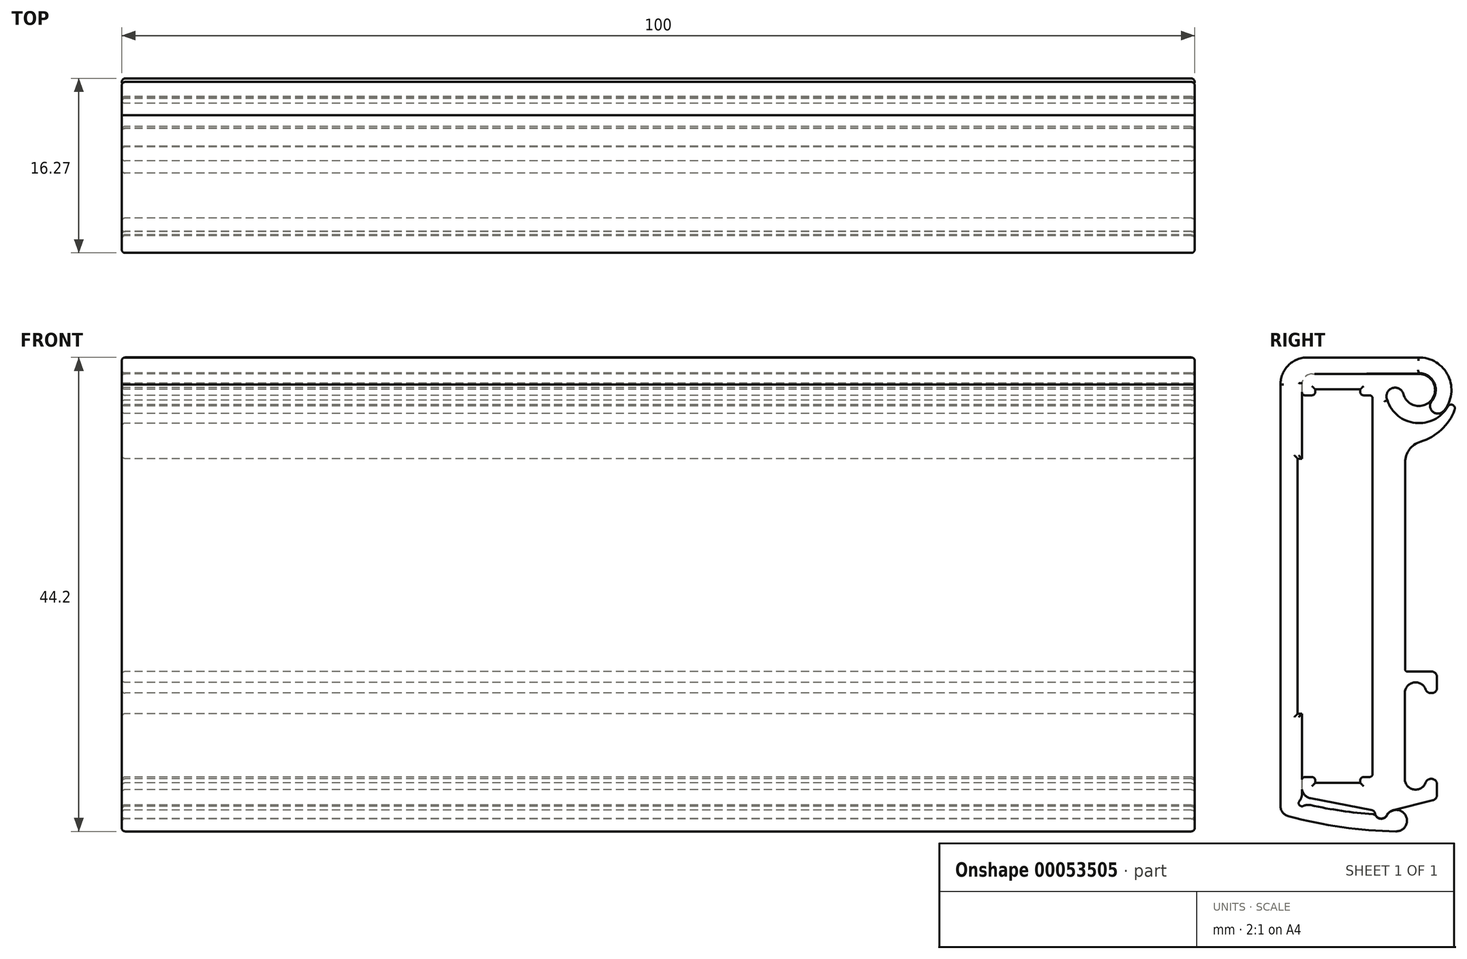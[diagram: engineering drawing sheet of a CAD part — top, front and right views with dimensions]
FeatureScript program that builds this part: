
annotation { "Feature Type Name" : "Feature", "Feature Type Description" : "" }
export const myFeature = defineFeature(function(context is Context, id is Id, definition is map)
    precondition{}
    {
        {
            var Q0;
            Q0=qCreatedBy(makeId("Right.planeOp"),FACE);
            var sketch = newSketch(context, id + "F0", { "sketchPlane" : qUnion([Q0])});
            skLineSegment(sketch, "E0.bottom", {"start": v(-0.5, 35) * mm, "end": v(-6, 35) * mm});
            skLineSegment(sketch, "E0.top", {"start": v(-0.5, 0) * mm, "end": v(-6, 0) * mm});
            skLineSegment(sketch, "E0.left", {"start": v(0, 34.5) * mm, "end": v(0, 0.5) * mm});
            skLineSegment(sketch, "E0.right", {"start": v(-6.5, 34.5) * mm, "end": v(-6.5, 0.5) * mm});
            skPoint(sketch, "E1.visualSharp", {"position": v(0, 35) * mm});
            skArc(sketch, "E1.filletArc", {"start": v(0, 34.5) * mm, "mid": v(-0.15, 34.85) * mm, "end": v(-0.5, 35) * mm});
            skPoint(sketch, "E2.visualSharp", {"position": v(-6.5, 35) * mm});
            skArc(sketch, "E2.filletArc", {"start": v(-6, 35) * mm, "mid": v(-6.35, 34.85) * mm, "end": v(-6.5, 34.5) * mm});
            skPoint(sketch, "E3.visualSharp", {"position": v(-6.5, 0) * mm});
            skArc(sketch, "E3.filletArc", {"start": v(-6.5, 0.5) * mm, "mid": v(-6.35, 0.15) * mm, "end": v(-6, 0) * mm});
            skPoint(sketch, "E4.visualSharp", {"position": v(0, 0) * mm});
            skArc(sketch, "E4.filletArc", {"start": v(-0.5, 0) * mm, "mid": v(-0.15, 0.15) * mm, "end": v(0, 0.5) * mm});
            skLineSegment(sketch, "E5", {"start": v(-6.5, 17.5) * mm, "end": v(0, 17.5) * mm, "construction": true});
            skLineSegment(sketch, "E6.rect.bottom", {"start": v(-3.25, 35.5) * mm, "end": v(-3.25, 35.5) * mm});
            skLineSegment(sketch, "E6.rect.top", {"start": v(-2.25, 34.5) * mm, "end": v(-4.25, 34.5) * mm, "construction": true});
            skLineSegment(sketch, "E6.rect.left", {"start": v(-2.25, 34.5) * mm, "end": v(-2.25, 34.5) * mm});
            skLineSegment(sketch, "E6.rect.right", {"start": v(-4.25, 34.5) * mm, "end": v(-4.25, 34.5) * mm});
            skPoint(sketch, "E6.rect.middle", {"position": v(-3.25, 35) * mm});
            skPoint(sketch, "E7.visualSharp", {"position": v(-4.25, 35.5) * mm});
            skArc(sketch, "E7.filletArc", {"start": v(-3.25, 35.5) * mm, "mid": v(-3.96, 35.2) * mm, "end": v(-4.25, 34.5) * mm, "construction": true});
            skPoint(sketch, "E8.visualSharp", {"position": v(-2.25, 35.5) * mm});
            skArc(sketch, "E8.filletArc", {"start": v(-2.25, 34.5) * mm, "mid": v(-2.54, 35.2) * mm, "end": v(-3.25, 35.5) * mm, "construction": true});
            skPoint(sketch, "E9.MirrorP", {"position": v(-3.25, 0) * mm});
            skPoint(sketch, "E10.MirrorP", {"position": v(-2.25, -0.5) * mm});
            skArc(sketch, "E11.MirrorCS", {"start": v(-2.25, 0.5) * mm, "mid": v(-2.54, -0.2) * mm, "end": v(-3.25, -0.5) * mm, "construction": true});
            skPoint(sketch, "E12.MirrorP", {"position": v(-4.25, -0.5) * mm});
            skLineSegment(sketch, "E13.MirrorCS", {"start": v(-3.25, -0.5) * mm, "end": v(-3.25, -0.5) * mm});
            skArc(sketch, "E14.MirrorCS", {"start": v(-3.25, -0.5) * mm, "mid": v(-3.96, -0.2) * mm, "end": v(-4.25, 0.5) * mm, "construction": true});
            skLineSegment(sketch, "E15.MirrorCS", {"start": v(-4.25, 0.5) * mm, "end": v(-4.25, 0.5) * mm});
            skLineSegment(sketch, "E16.MirrorCS", {"start": v(-2.25, 0.5) * mm, "end": v(-4.25, 0.5) * mm, "construction": true});
            skLineSegment(sketch, "E17.MirrorCS", {"start": v(-2.25, 0.5) * mm, "end": v(-2.25, 0.5) * mm});
            skLineSegment(sketch, "E18.rect.bottom", {"start": v(-6, 29.4) * mm, "end": v(-6.5, 29.4) * mm});
            skLineSegment(sketch, "E18.rect.top", {"start": v(-6, 5.6) * mm, "end": v(-6.5, 5.6) * mm});
            skLineSegment(sketch, "E18.rect.left", {"start": v(-6, 29.4) * mm, "end": v(-6, 5.6) * mm, "construction": true});
            skPoint(sketch, "E18.rect.middle", {"position": v(-6.5, 17.5) * mm});
            skPoint(sketch, "E18.rect.right.end.orphan", {"position": v(-7, 5.6) * mm});
            skPoint(sketch, "E18.rect.right.start.orphan", {"position": v(-7, 29.4) * mm});
            skSolve(sketch);
        }
        {
            var Q0;
            Q0=qCreatedBy(makeId("Right.planeOp"),FACE);
            var sketch = newSketch(context, id + "F1", { "sketchPlane" : qUnion([Q0])});
            skLineSegment(sketch, "E19", {"start": v(-6.3, 35.3) * mm, "end": v(-5.65, 35.3) * mm});
            skLineSegment(sketch, "E20", {"start": v(0, 35) * mm, "end": v(0, 0) * mm});
            skLineSegment(sketch, "E21", {"start": v(-0.3, -0.3) * mm, "end": v(-0.85, -0.3) * mm});
            skLineSegment(sketch, "E22", {"start": v(-12.05, -2.3) * mm, "end": v(-5.6, -2.3) * mm, "construction": true});
            skLineSegment(sketch, "E23", {"start": v(-5.35, 35.6) * mm, "end": v(-5.35, 35.85) * mm});
            skLineSegment(sketch, "E24", {"start": v(-5.35, 35.85) * mm, "end": v(-1.15, 35.85) * mm});
            skLineSegment(sketch, "E25", {"start": v(-1.15, 35.85) * mm, "end": v(-1.15, 35.6) * mm});
            skLineSegment(sketch, "E26.trimOffspring", {"start": v(-0.85, 35.3) * mm, "end": v(-0.3, 35.3) * mm});
            skLineSegment(sketch, "E27.MirrorCS", {"start": v(-1.15, -0.85) * mm, "end": v(-1.15, -0.6) * mm});
            skLineSegment(sketch, "E28.MirrorCS", {"start": v(-5.35, -0.6) * mm, "end": v(-5.35, -0.85) * mm});
            skLineSegment(sketch, "E29.MirrorCS", {"start": v(-5.35, -0.85) * mm, "end": v(-1.15, -0.85) * mm});
            skLineSegment(sketch, "E30.trimOffspring", {"start": v(-5.65, -0.3) * mm, "end": v(-6.3, -0.3) * mm});
            skPoint(sketch, "E31.visualSharp", {"position": v(-6, 35.3) * mm});
            skArc(sketch, "E31.filletArc", {"start": v(-6.6, 35.6) * mm, "mid": v(-6.51, 35.39) * mm, "end": v(-6.3, 35.3) * mm});
            skPoint(sketch, "E32.visualSharp", {"position": v(-5.35, 35.3) * mm});
            skArc(sketch, "E32.filletArc", {"start": v(-5.65, 35.3) * mm, "mid": v(-5.44, 35.39) * mm, "end": v(-5.35, 35.6) * mm});
            skPoint(sketch, "E33.visualSharp", {"position": v(0, 35.3) * mm});
            skArc(sketch, "E33.filletArc", {"start": v(0, 35) * mm, "mid": v(-0.09, 35.21) * mm, "end": v(-0.3, 35.3) * mm});
            skPoint(sketch, "E34.visualSharp", {"position": v(-1.15, 35.3) * mm});
            skArc(sketch, "E34.filletArc", {"start": v(-1.15, 35.6) * mm, "mid": v(-1.06, 35.39) * mm, "end": v(-0.85, 35.3) * mm});
            skPoint(sketch, "E35.visualSharp", {"position": v(-6, -0.3) * mm});
            skArc(sketch, "E35.filletArc", {"start": v(-6.3, -0.3) * mm, "mid": v(-6.51, -0.39) * mm, "end": v(-6.6, -0.6) * mm});
            skPoint(sketch, "E36.visualSharp", {"position": v(-5.35, -0.3) * mm});
            skArc(sketch, "E36.filletArc", {"start": v(-5.35, -0.6) * mm, "mid": v(-5.44, -0.39) * mm, "end": v(-5.65, -0.3) * mm});
            skPoint(sketch, "E37.visualSharp", {"position": v(-1.15, -0.3) * mm});
            skArc(sketch, "E37.filletArc", {"start": v(-0.85, -0.3) * mm, "mid": v(-1.06, -0.39) * mm, "end": v(-1.15, -0.6) * mm});
            skPoint(sketch, "E38.visualSharp", {"position": v(0, -0.3) * mm});
            skArc(sketch, "E38.filletArc", {"start": v(-0.3, -0.3) * mm, "mid": v(-0.09, -0.21) * mm, "end": v(0, 0) * mm});
            skPoint(sketch, "E39.visualSharp", {"position": v(1.45, 37.5) * mm});
            skPoint(sketch, "E40.visualSharp", {"position": v(-6, 37.5) * mm});
            skArc(sketch, "E40.filletArc", {"start": v(-5.6, 37.3) * mm, "mid": v(-6.3, 37) * mm, "end": v(-6.6, 36.3) * mm});
            skPoint(sketch, "E41.visualSharp", {"position": v(-6, -2.3) * mm});
            skArc(sketch, "E41.filletArc", {"start": v(-6.6, -1.3) * mm, "mid": v(-6.37, -1.94) * mm, "end": v(-5.79, -2.28) * mm});
            skArc(sketch, "E42", {"start": v(4.02, -3.35) * mm, "mid": v(-6.17, -2.3) * mm, "end": v(-15.75, 1.34) * mm, "construction": true});
            skLineSegment(sketch, "E43", {"start": v(-5.79, -2.28) * mm, "end": v(-0.09, -3.38) * mm});
            skArc(sketch, "E44", {"start": v(0.23, -3.7) * mm, "mid": v(0.7, -4.17) * mm, "end": v(1.31, -3.87) * mm});
            skPoint(sketch, "E45.visualSharp", {"position": v(0.24, -3.44) * mm});
            skArc(sketch, "E45.filletArc", {"start": v(0.23, -3.7) * mm, "mid": v(0.12, -3.49) * mm, "end": v(-0.09, -3.38) * mm});
            skPoint(sketch, "E46.visualSharp", {"position": v(1.32, -3.33) * mm});
            skPoint(sketch, "E47.visualSharp", {"position": v(-12.05, -2.3) * mm});
            skLineSegment(sketch, "E48", {"start": v(7.02, 35.23) * mm, "end": v(7.02, -7.2) * mm, "construction": true});
            skLineSegment(sketch, "E49", {"start": v(5.5, 9.53) * mm, "end": v(3.23, 9.53) * mm});
            skPoint(sketch, "E50.visualSharp", {"position": v(7.02, 9.53) * mm});
            skLineSegment(sketch, "E51.trimOffspring", {"start": v(3.03, 9.73) * mm, "end": v(3.03, 29.06) * mm});
            skPoint(sketch, "E52.visualSharp", {"position": v(7.02, 6.35) * mm});
            skPoint(sketch, "E53.visualSharp", {"position": v(3.03, 9.53) * mm});
            skArc(sketch, "E53.filletArc", {"start": v(3.03, 9.73) * mm, "mid": v(3.1, 9.6) * mm, "end": v(3.23, 9.53) * mm});
            skLineSegment(sketch, "E54", {"start": v(6, 9.03) * mm, "end": v(6, 8.03) * mm});
            skLineSegment(sketch, "E55", {"start": v(5.5, 7.53) * mm, "end": v(5.41, 7.53) * mm});
            skLineSegment(sketch, "E56", {"start": v(3, 7.53) * mm, "end": v(3, -0.47) * mm});
            skLineSegment(sketch, "E57", {"start": v(5.41, -0.47) * mm, "end": v(5.5, -0.47) * mm});
            skArc(sketch, "E58", {"start": v(3, 7.53) * mm, "mid": v(3.83, 8.51) * mm, "end": v(4.94, 7.86) * mm});
            skArc(sketch, "E59", {"start": v(3, -0.47) * mm, "mid": v(3.83, -1.46) * mm, "end": v(4.94, -0.8) * mm});
            skPoint(sketch, "E60.visualSharp", {"position": v(5, 7.53) * mm});
            skArc(sketch, "E60.filletArc", {"start": v(4.94, 7.86) * mm, "mid": v(5.13, 7.62) * mm, "end": v(5.41, 7.53) * mm});
            skPoint(sketch, "E61.newPointA", {"position": v(7, 7.53) * mm});
            skArc(sketch, "E61.filletArc", {"start": v(5.5, 7.53) * mm, "mid": v(5.85, 7.67) * mm, "end": v(6, 8.03) * mm});
            skPoint(sketch, "E62.visualSharp", {"position": v(5, -0.47) * mm});
            skArc(sketch, "E62.filletArc", {"start": v(5.41, -0.47) * mm, "mid": v(5.13, -0.57) * mm, "end": v(4.94, -0.8) * mm});
            skLineSegment(sketch, "E63", {"start": v(6, -0.97) * mm, "end": v(6, -1.98) * mm});
            skPoint(sketch, "E64.visualSharp", {"position": v(6, -0.47) * mm});
            skArc(sketch, "E64.filletArc", {"start": v(6, -0.97) * mm, "mid": v(5.85, -0.62) * mm, "end": v(5.5, -0.47) * mm});
            skPoint(sketch, "E65.visualSharp", {"position": v(6, 9.53) * mm});
            skArc(sketch, "E65.filletArc", {"start": v(6, 9.03) * mm, "mid": v(5.85, 9.39) * mm, "end": v(5.5, 9.53) * mm});
            skPoint(sketch, "E66.visualSharp", {"position": v(4.49, 37.5) * mm});
            skPoint(sketch, "E67.visualSharp", {"position": v(7.02, 37.73) * mm});
            skLineSegment(sketch, "E68.bottom", {"start": v(-5.35, 35.85) * mm, "end": v(-1.15, 35.85) * mm, "construction": true});
            skLineSegment(sketch, "E68.top", {"start": v(-5.35, 35.5) * mm, "end": v(-1.15, 35.5) * mm, "construction": true});
            skLineSegment(sketch, "E68.left", {"start": v(-5.35, 35.85) * mm, "end": v(-5.35, 35.5) * mm, "construction": true});
            skLineSegment(sketch, "E68.right", {"start": v(-1.15, 35.85) * mm, "end": v(-1.15, 35.5) * mm, "construction": true});
            skLineSegment(sketch, "E69", {"start": v(-5.6, 37.3) * mm, "end": v(4.32, 37.3) * mm});
            skLineSegment(sketch, "E70", {"start": v(-6.6, 36.3) * mm, "end": v(-6.6, 35.6) * mm});
            skLineSegment(sketch, "E71", {"start": v(-3.25, 35.85) * mm, "end": v(-3.25, 34.98) * mm, "construction": true});
            skPoint(sketch, "E71.endSnap0", {"position": v(-3.25, 35.85) * mm});
            skLineSegment(sketch, "E72", {"start": v(-6.6, -0.6) * mm, "end": v(-6.6, -1.3) * mm});
            skArc(sketch, "E73", {"start": v(4.32, 37.3) * mm, "mid": v(5.5, 34.89) * mm, "end": v(2.87, 35.41) * mm});
            skArc(sketch, "E74", {"start": v(1.37, 34.84) * mm, "mid": v(4, 32.72) * mm, "end": v(7, 34.25) * mm});
            skArc(sketch, "E75", {"start": v(2.87, 35.41) * mm, "mid": v(1.8, 35.96) * mm, "end": v(1.37, 34.84) * mm});
            skLineSegment(sketch, "E76", {"start": v(4.32, 35.8) * mm, "end": v(7.3, 35.8) * mm, "construction": true});
            skPoint(sketch, "E77.startSnap0", {"position": v(5.5, 34.89) * mm});
            skArc(sketch, "E78", {"start": v(4.46, 30.97) * mm, "mid": v(6.4, 32.08) * mm, "end": v(7.65, 33.94) * mm});
            skLineSegment(sketch, "E79", {"start": v(3.03, 31.44) * mm, "end": v(3.03, 35.7) * mm, "construction": true});
            skArc(sketch, "E80", {"start": v(7, 34.25) * mm, "mid": v(7.47, 34.4) * mm, "end": v(7.65, 33.94) * mm});
            skPoint(sketch, "E81.visualSharp", {"position": v(3.03, 30.76) * mm});
            skArc(sketch, "E81.filletArc", {"start": v(4.46, 30.97) * mm, "mid": v(3.43, 30.25) * mm, "end": v(3.03, 29.06) * mm});
            skLineSegment(sketch, "E82", {"start": v(4.32, 35.8) * mm, "end": v(2.1, 35.2) * mm, "construction": true});
            skArc(sketch, "E83", {"start": v(1.31, -3.87) * mm, "mid": v(1.58, -3.56) * mm, "end": v(1.96, -3.38) * mm});
            skLineSegment(sketch, "E84", {"start": v(1.96, -3.38) * mm, "end": v(5.62, -2.47) * mm});
            skPoint(sketch, "E85.visualSharp", {"position": v(6, -2.37) * mm});
            skArc(sketch, "E85.filletArc", {"start": v(5.62, -2.47) * mm, "mid": v(5.9, -2.29) * mm, "end": v(6, -1.98) * mm});
            skLineSegment(sketch, "E86", {"start": v(4.32, 35.8) * mm, "end": v(7.32, 34.07) * mm, "construction": true});
            skSolve(sketch);
        }
        {
            var Q0;
            Q0=qCreatedBy(makeId("Right.planeOp"),FACE);
            var sketch = newSketch(context, id + "F2", { "sketchPlane" : qUnion([Q0])});
            skArc(sketch, "E87.2", {"start": v(-5.6, 37.3) * mm, "mid": v(-6.26, 37.05) * mm, "end": v(-6.6, 36.43) * mm});
            skLineSegment(sketch, "E87.3", {"start": v(-5.6, 37.3) * mm, "end": v(4.26, 37.37) * mm});
            skArc(sketch, "E88.1", {"start": v(-6.1, 38.83) * mm, "mid": v(-7.87, 38.09) * mm, "end": v(-8.6, 36.3) * mm});
            skLineSegment(sketch, "E89", {"start": v(-8.6, 36.3) * mm, "end": v(-8.6, -3) * mm});
            skPoint(sketch, "E90.visualSharp", {"position": v(-6.03, 35.1) * mm});
            skArc(sketch, "E91", {"start": v(-5.8, -2.92) * mm, "mid": v(-2.9, -3.45) * mm, "end": v(0.01, -3.77) * mm});
            skArc(sketch, "E92.0", {"start": v(-7.85, -3.96) * mm, "mid": v(-2.87, -4.97) * mm, "end": v(2.19, -5.37) * mm});
            skPoint(sketch, "E93.trimOffspring.end.orphan", {"position": v(-7.6, -5.55) * mm});
            skPoint(sketch, "E94.orphan", {"position": v(-8.6, -5.55) * mm});
            skPoint(sketch, "E95.visualSharp", {"position": v(-8.6, -3.75) * mm});
            skArc(sketch, "E95.filletArc", {"start": v(-8.6, -3) * mm, "mid": v(-8.38, -3.6) * mm, "end": v(-7.85, -3.96) * mm});
            skPoint(sketch, "E96.visualSharp", {"position": v(12.44, -2.73) * mm});
            skLineSegment(sketch, "E97.0", {"start": v(-6.6, 36.43) * mm, "end": v(-6.6, 29.4) * mm});
            skArc(sketch, "E98", {"start": v(-6.82, -2.54) * mm, "mid": v(-6.83, -2.92) * mm, "end": v(-6.46, -3) * mm});
            skPoint(sketch, "E99.visualSharp", {"position": v(-6.6, -2.43) * mm});
            skArc(sketch, "E99.filletArc", {"start": v(-6.82, -2.54) * mm, "mid": v(-6.65, -2.24) * mm, "end": v(-6.6, -1.9) * mm});
            skPoint(sketch, "E100.visualSharp", {"position": v(-6.3, -2.8) * mm});
            skArc(sketch, "E100.filletArc", {"start": v(-5.8, -2.92) * mm, "mid": v(-6.13, -2.9) * mm, "end": v(-6.46, -3) * mm});
            skPoint(sketch, "E101.visualSharp", {"position": v(0.78, -3.82) * mm});
            skLineSegment(sketch, "E102", {"start": v(-6.6, 29.4) * mm, "end": v(-7, 29.4) * mm});
            skLineSegment(sketch, "E103", {"start": v(-6.6, 5.6) * mm, "end": v(-7, 5.6) * mm});
            skLineSegment(sketch, "E104", {"start": v(-7, 5.6) * mm, "end": v(-7, 29.4) * mm});
            skLineSegment(sketch, "E105.trimOffspring", {"start": v(-6.6, 5.6) * mm, "end": v(-6.6, -1.9) * mm});
            skLineSegment(sketch, "E106", {"start": v(-6.1, 38.83) * mm, "end": v(4.26, 38.83) * mm});
            skArc(sketch, "E107", {"start": v(1.33, -3.88) * mm, "mid": v(3.07, -3.87) * mm, "end": v(2.19, -5.37) * mm});
            skArc(sketch, "E108", {"start": v(0.31, -3.94) * mm, "mid": v(0.83, -4.2) * mm, "end": v(1.33, -3.88) * mm});
            skPoint(sketch, "E109.visualSharp", {"position": v(0.23, -3.78) * mm});
            skArc(sketch, "E109.filletArc", {"start": v(0.31, -3.94) * mm, "mid": v(0.18, -3.82) * mm, "end": v(0.01, -3.77) * mm});
            skArc(sketch, "E110.0", {"start": v(4.26, 37.37) * mm, "mid": v(5.73, 36.49) * mm, "end": v(5.52, 34.8) * mm});
            skArc(sketch, "E111.0", {"start": v(6.64, 33.85) * mm, "mid": v(7.05, 37.1) * mm, "end": v(4.26, 38.83) * mm});
            skLineSegment(sketch, "E112", {"start": v(4.32, 35.8) * mm, "end": v(6.64, 33.85) * mm, "construction": true});
            skArc(sketch, "E113", {"start": v(5.52, 34.8) * mm, "mid": v(5.61, 33.76) * mm, "end": v(6.64, 33.85) * mm});
            skSolve(sketch);
        }
        {
            var Q0;
            Q0=qSketchRegion(id+"F1",true);
            extrude(context, id + "F3", {"entities" : qUnion([Q0]), "depth" : 100 * mm});
        }
        {
            var Q0;
            Q0 = qSketchRegion(id + "F2", true);
            extrude(context, id + "F4", {"entities" : qUnion([Q0]), "depth" : 100 * mm});
        }
        {
            var Q0;
            Q0=makeQuery(id+"F4.opExtrude","CAP_FACE",FACE,{"disambiguationData":[OSD([sQuery(id+"F2.wireOp",EDGE,"E87.2"),sQuery(id+"F2.wireOp",EDGE,"E87.3"),sQuery(id+"F2.wireOp",EDGE,"E88.1"),sQuery(id+"F2.wireOp",EDGE,"E89"),sQuery(id+"F2.wireOp",EDGE,"E91"),sQuery(id+"F2.wireOp",EDGE,"E92.0"),sQuery(id+"F2.wireOp",EDGE,"E95.filletArc"),sQuery(id+"F2.wireOp",EDGE,"E97.0"),sQuery(id+"F2.wireOp",EDGE,"E98"),sQuery(id+"F2.wireOp",EDGE,"E99.filletArc"),sQuery(id+"F2.wireOp",EDGE,"E100.filletArc"),sQuery(id+"F2.wireOp",EDGE,"E102"),sQuery(id+"F2.wireOp",EDGE,"E103"),sQuery(id+"F2.wireOp",EDGE,"E104"),sQuery(id+"F2.wireOp",EDGE,"E105.trimOffspring"),sQuery(id+"F2.wireOp",EDGE,"E106"),sQuery(id+"F2.wireOp",EDGE,"E107"),sQuery(id+"F2.wireOp",EDGE,"E108"),sQuery(id+"F2.wireOp",EDGE,"E109.filletArc"),sQuery(id+"F2.wireOp",EDGE,"E110.0"),sQuery(id+"F2.wireOp",EDGE,"E111.0"),sQuery(id+"F2.wireOp",EDGE,"E113")])],"isStart":false});
            var Q1;
            Q1=makeQuery(id+"F4.opExtrude","CAP_FACE",FACE,{"disambiguationData":[OSD([sQuery(id+"F2.wireOp",EDGE,"E87.2"),sQuery(id+"F2.wireOp",EDGE,"E87.3"),sQuery(id+"F2.wireOp",EDGE,"E88.1"),sQuery(id+"F2.wireOp",EDGE,"E89"),sQuery(id+"F2.wireOp",EDGE,"E91"),sQuery(id+"F2.wireOp",EDGE,"E92.0"),sQuery(id+"F2.wireOp",EDGE,"E95.filletArc"),sQuery(id+"F2.wireOp",EDGE,"E97.0"),sQuery(id+"F2.wireOp",EDGE,"E98"),sQuery(id+"F2.wireOp",EDGE,"E99.filletArc"),sQuery(id+"F2.wireOp",EDGE,"E100.filletArc"),sQuery(id+"F2.wireOp",EDGE,"E102"),sQuery(id+"F2.wireOp",EDGE,"E103"),sQuery(id+"F2.wireOp",EDGE,"E104"),sQuery(id+"F2.wireOp",EDGE,"E105.trimOffspring"),sQuery(id+"F2.wireOp",EDGE,"E106"),sQuery(id+"F2.wireOp",EDGE,"E107"),sQuery(id+"F2.wireOp",EDGE,"E108"),sQuery(id+"F2.wireOp",EDGE,"E109.filletArc"),sQuery(id+"F2.wireOp",EDGE,"E110.0"),sQuery(id+"F2.wireOp",EDGE,"E111.0"),sQuery(id+"F2.wireOp",EDGE,"E113")])],"isStart":true});
            fillet(context, id + "F5", {"entities" : qUnion([Q0, Q1]), "radius" : .3 * mm, "tangentPropagation" : true, "allowEdgeOverflow" : false});
        }
        {
            var Q0;
            Q0=makeQuery(id+"F3.opExtrude","CAP_FACE",FACE,{"disambiguationData":[OSD([sQuery(id+"F1.wireOp",EDGE,"E19"),sQuery(id+"F1.wireOp",EDGE,"E20"),sQuery(id+"F1.wireOp",EDGE,"E21"),sQuery(id+"F1.wireOp",EDGE,"E23"),sQuery(id+"F1.wireOp",EDGE,"E24"),sQuery(id+"F1.wireOp",EDGE,"E25"),sQuery(id+"F1.wireOp",EDGE,"E26.trimOffspring"),sQuery(id+"F1.wireOp",EDGE,"E27.MirrorCS"),sQuery(id+"F1.wireOp",EDGE,"E28.MirrorCS"),sQuery(id+"F1.wireOp",EDGE,"E29.MirrorCS"),sQuery(id+"F1.wireOp",EDGE,"E30.trimOffspring"),sQuery(id+"F1.wireOp",EDGE,"E31.filletArc"),sQuery(id+"F1.wireOp",EDGE,"E32.filletArc"),sQuery(id+"F1.wireOp",EDGE,"E33.filletArc"),sQuery(id+"F1.wireOp",EDGE,"E34.filletArc"),sQuery(id+"F1.wireOp",EDGE,"E35.filletArc"),sQuery(id+"F1.wireOp",EDGE,"E36.filletArc"),sQuery(id+"F1.wireOp",EDGE,"E37.filletArc"),sQuery(id+"F1.wireOp",EDGE,"E38.filletArc"),sQuery(id+"F1.wireOp",EDGE,"E40.filletArc"),sQuery(id+"F1.wireOp",EDGE,"E41.filletArc"),sQuery(id+"F1.wireOp",EDGE,"E43"),sQuery(id+"F1.wireOp",EDGE,"E44"),sQuery(id+"F1.wireOp",EDGE,"E45.filletArc"),sQuery(id+"F1.wireOp",EDGE,"E49"),sQuery(id+"F1.wireOp",EDGE,"E51.trimOffspring"),sQuery(id+"F1.wireOp",EDGE,"E53.filletArc"),sQuery(id+"F1.wireOp",EDGE,"E54"),sQuery(id+"F1.wireOp",EDGE,"E55"),sQuery(id+"F1.wireOp",EDGE,"E56"),sQuery(id+"F1.wireOp",EDGE,"E57"),sQuery(id+"F1.wireOp",EDGE,"E58"),sQuery(id+"F1.wireOp",EDGE,"E59"),sQuery(id+"F1.wireOp",EDGE,"E60.filletArc"),sQuery(id+"F1.wireOp",EDGE,"E61.filletArc"),sQuery(id+"F1.wireOp",EDGE,"E62.filletArc"),sQuery(id+"F1.wireOp",EDGE,"E63"),sQuery(id+"F1.wireOp",EDGE,"E64.filletArc"),sQuery(id+"F1.wireOp",EDGE,"E65.filletArc"),sQuery(id+"F1.wireOp",EDGE,"E69"),sQuery(id+"F1.wireOp",EDGE,"E70"),sQuery(id+"F1.wireOp",EDGE,"E72"),sQuery(id+"F1.wireOp",EDGE,"E73"),sQuery(id+"F1.wireOp",EDGE,"E74"),sQuery(id+"F1.wireOp",EDGE,"E75"),sQuery(id+"F1.wireOp",EDGE,"E78"),sQuery(id+"F1.wireOp",EDGE,"E80"),sQuery(id+"F1.wireOp",EDGE,"E81.filletArc"),sQuery(id+"F1.wireOp",EDGE,"E83"),sQuery(id+"F1.wireOp",EDGE,"E84"),sQuery(id+"F1.wireOp",EDGE,"E85.filletArc")])],"isStart":false});
            var Q1;
            Q1=makeQuery(id+"F3.opExtrude","CAP_FACE",FACE,{"disambiguationData":[OSD([sQuery(id+"F1.wireOp",EDGE,"E19"),sQuery(id+"F1.wireOp",EDGE,"E20"),sQuery(id+"F1.wireOp",EDGE,"E21"),sQuery(id+"F1.wireOp",EDGE,"E23"),sQuery(id+"F1.wireOp",EDGE,"E24"),sQuery(id+"F1.wireOp",EDGE,"E25"),sQuery(id+"F1.wireOp",EDGE,"E26.trimOffspring"),sQuery(id+"F1.wireOp",EDGE,"E27.MirrorCS"),sQuery(id+"F1.wireOp",EDGE,"E28.MirrorCS"),sQuery(id+"F1.wireOp",EDGE,"E29.MirrorCS"),sQuery(id+"F1.wireOp",EDGE,"E30.trimOffspring"),sQuery(id+"F1.wireOp",EDGE,"E31.filletArc"),sQuery(id+"F1.wireOp",EDGE,"E32.filletArc"),sQuery(id+"F1.wireOp",EDGE,"E33.filletArc"),sQuery(id+"F1.wireOp",EDGE,"E34.filletArc"),sQuery(id+"F1.wireOp",EDGE,"E35.filletArc"),sQuery(id+"F1.wireOp",EDGE,"E36.filletArc"),sQuery(id+"F1.wireOp",EDGE,"E37.filletArc"),sQuery(id+"F1.wireOp",EDGE,"E38.filletArc"),sQuery(id+"F1.wireOp",EDGE,"E40.filletArc"),sQuery(id+"F1.wireOp",EDGE,"E41.filletArc"),sQuery(id+"F1.wireOp",EDGE,"E43"),sQuery(id+"F1.wireOp",EDGE,"E44"),sQuery(id+"F1.wireOp",EDGE,"E45.filletArc"),sQuery(id+"F1.wireOp",EDGE,"E49"),sQuery(id+"F1.wireOp",EDGE,"E51.trimOffspring"),sQuery(id+"F1.wireOp",EDGE,"E53.filletArc"),sQuery(id+"F1.wireOp",EDGE,"E54"),sQuery(id+"F1.wireOp",EDGE,"E55"),sQuery(id+"F1.wireOp",EDGE,"E56"),sQuery(id+"F1.wireOp",EDGE,"E57"),sQuery(id+"F1.wireOp",EDGE,"E58"),sQuery(id+"F1.wireOp",EDGE,"E59"),sQuery(id+"F1.wireOp",EDGE,"E60.filletArc"),sQuery(id+"F1.wireOp",EDGE,"E61.filletArc"),sQuery(id+"F1.wireOp",EDGE,"E62.filletArc"),sQuery(id+"F1.wireOp",EDGE,"E63"),sQuery(id+"F1.wireOp",EDGE,"E64.filletArc"),sQuery(id+"F1.wireOp",EDGE,"E65.filletArc"),sQuery(id+"F1.wireOp",EDGE,"E69"),sQuery(id+"F1.wireOp",EDGE,"E70"),sQuery(id+"F1.wireOp",EDGE,"E72"),sQuery(id+"F1.wireOp",EDGE,"E73"),sQuery(id+"F1.wireOp",EDGE,"E74"),sQuery(id+"F1.wireOp",EDGE,"E75"),sQuery(id+"F1.wireOp",EDGE,"E78"),sQuery(id+"F1.wireOp",EDGE,"E80"),sQuery(id+"F1.wireOp",EDGE,"E81.filletArc"),sQuery(id+"F1.wireOp",EDGE,"E83"),sQuery(id+"F1.wireOp",EDGE,"E84"),sQuery(id+"F1.wireOp",EDGE,"E85.filletArc")])],"isStart":true});
            fillet(context, id + "F6", {"entities" : qUnion([Q0, Q1]), "radius" : .3 * mm, "tangentPropagation" : true, "allowEdgeOverflow" : false});
        }
    });
